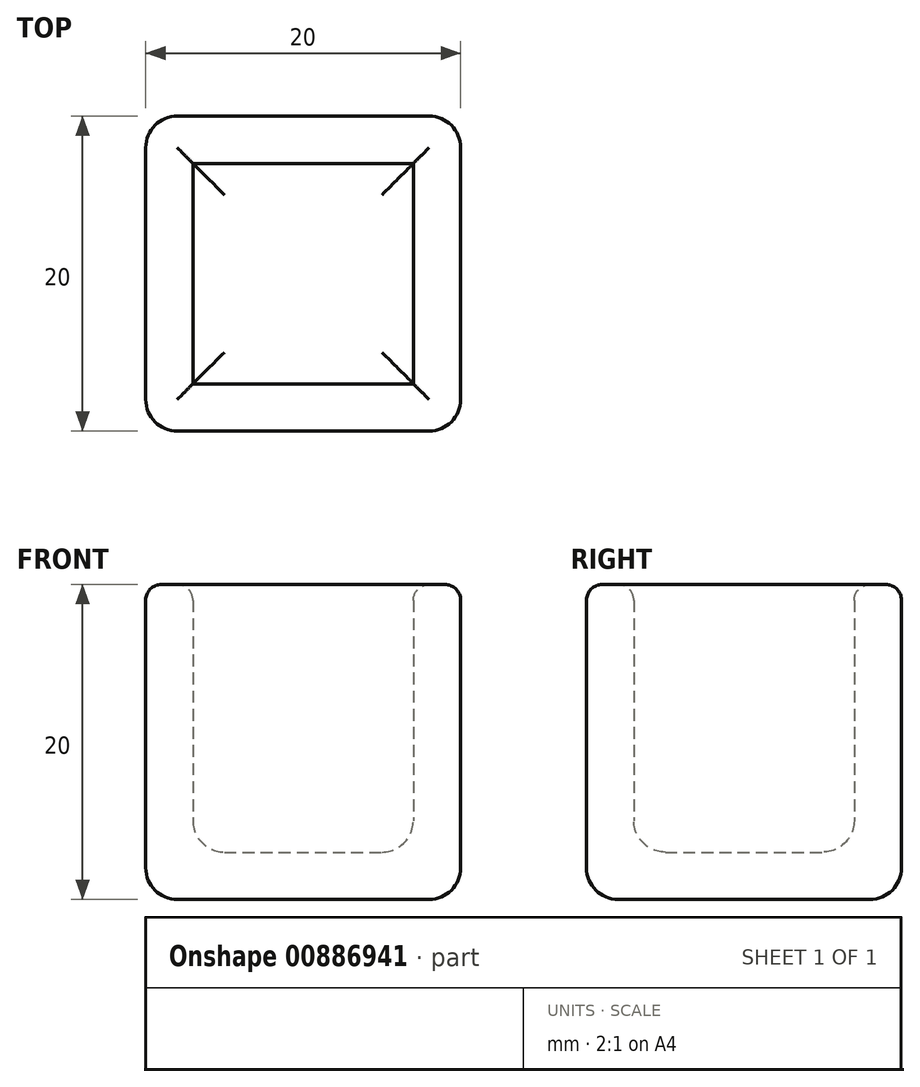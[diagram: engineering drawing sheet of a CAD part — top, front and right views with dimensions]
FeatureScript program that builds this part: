
annotation { "Feature Type Name" : "Feature", "Feature Type Description" : "" }
export const myFeature = defineFeature(function(context is Context, id is Id, definition is map)
    precondition{}
    {
        {
            var Q0;
            Q0=qCreatedBy(makeId("Top.planeOp"),FACE);
            var sketch = newSketch(context, id + "F0", { "sketchPlane" : qUnion([Q0])});
            skLineSegment(sketch, "E0.bottom", {"start": v(-8, 10) * mm, "end": v(8, 10) * mm});
            skLineSegment(sketch, "E0.top", {"start": v(-8, -10) * mm, "end": v(8, -10) * mm});
            skLineSegment(sketch, "E0.left", {"start": v(-10, 8) * mm, "end": v(-10, -8) * mm});
            skLineSegment(sketch, "E0.right", {"start": v(10, 8) * mm, "end": v(10, -8) * mm});
            skPoint(sketch, "E0.middle", {"position": v(0, 0) * mm});
            skPoint(sketch, "E1.visualSharp", {"position": v(-10, 10) * mm});
            skArc(sketch, "E1.filletArc", {"start": v(-8, 10) * mm, "mid": v(-9.41, 9.41) * mm, "end": v(-10, 8) * mm});
            skPoint(sketch, "E2.visualSharp", {"position": v(10, 10) * mm});
            skArc(sketch, "E2.filletArc", {"start": v(10, 8) * mm, "mid": v(9.41, 9.41) * mm, "end": v(8, 10) * mm});
            skPoint(sketch, "E3.visualSharp", {"position": v(10, -10) * mm});
            skArc(sketch, "E3.filletArc", {"start": v(8, -10) * mm, "mid": v(9.41, -9.41) * mm, "end": v(10, -8) * mm});
            skPoint(sketch, "E4.visualSharp", {"position": v(-10, -10) * mm});
            skArc(sketch, "E4.filletArc", {"start": v(-10, -8) * mm, "mid": v(-9.41, -9.41) * mm, "end": v(-8, -10) * mm});
            skSolve(sketch);
        }
        {
            var Q0;
            Q0=makeQuery(id+"F0.imprint","IMPRINT",FACE,{"disambiguationData":[TD([[makeQuery(id+"F0.imprint","IMPRINT",EDGE,{"derivedFrom":sQuery(id+"F0.wireOp",EDGE,"E0.bottom")}),-1.0]])]});
            extrude(context, id + "F1", {"entities" : qUnion([Q0]), "depth" : 20 * mm, "offsetDistance" : 25 * mm});
        }
        {
            var Q0;
            Q0=makeQuery(id+"F1.opExtrude","CAP_EDGE",EDGE,{"disambiguationData":[OSD([sQuery(id+"F0.wireOp",EDGE,"E0.top")])],"isStart":true});
            fillet(context, id + "F2", {"entities" : qUnion([Q0]), "radius" : 2 * mm, "tangentPropagation" : true, "allowEdgeOverflow" : false});
        }
        {
            var Q0;
            Q0=makeQuery(id+"F1.opExtrude","CAP_FACE",FACE,{"disambiguationData":[OSD([sQuery(id+"F0.wireOp",EDGE,"E0.bottom"),sQuery(id+"F0.wireOp",EDGE,"E0.top"),sQuery(id+"F0.wireOp",EDGE,"E0.left"),sQuery(id+"F0.wireOp",EDGE,"E0.right"),sQuery(id+"F0.wireOp",EDGE,"E1.filletArc"),sQuery(id+"F0.wireOp",EDGE,"E2.filletArc"),sQuery(id+"F0.wireOp",EDGE,"E3.filletArc"),sQuery(id+"F0.wireOp",EDGE,"E4.filletArc")])],"isStart":false});
            shell(context, id + "F3", {"entities" : qUnion([Q0]), "thickness" : 3 * mm});
        }
        {
            var Q0;
            Q0=makeQuery(id+"F1.opExtrude","CAP_EDGE",EDGE,{"disambiguationData":[OSD([sQuery(id+"F0.wireOp",EDGE,"E0.left")])],"isStart":false});
            var Q1;
            Q1=makeQuery(id+"F3.opShell","OFFSET_EDGE",EDGE,{"disambiguationData":[OSD([sQuery(id+"F0.wireOp",EDGE,"E0.right")])]});
            var Q2;
            Q2=makeQuery(id+"F3.opShell","OFFSET_EDGE",EDGE,{"disambiguationData":[OSD([sQuery(id+"F0.wireOp",EDGE,"E0.bottom")])]});
            var Q3;
            Q3=makeQuery(id+"F3.opShell","OFFSET_EDGE",EDGE,{"disambiguationData":[OSD([sQuery(id+"F0.wireOp",EDGE,"E0.left")])]});
            var Q4;
            Q4=makeQuery(id+"F3.opShell","OFFSET_EDGE",EDGE,{"disambiguationData":[OSD([sQuery(id+"F0.wireOp",EDGE,"E0.top")])]});
            fillet(context, id + "F4", {"entities" : qUnion([Q0, Q1, Q2, Q3, Q4]), "radius" : 1 * mm, "tangentPropagation" : true, "allowEdgeOverflow" : false});
        }
        {
            var Q0;
            {var subQ0=sQuery(id+"F0.wireOp",EDGE,"E4.filletArc");var subQ1=sQuery(id+"F0.wireOp",EDGE,"E3.filletArc");var subQ2=sQuery(id+"F0.wireOp",EDGE,"E2.filletArc");var subQ3=sQuery(id+"F0.wireOp",EDGE,"E1.filletArc");var subQ4=sQuery(id+"F0.wireOp",EDGE,"E0.right");var subQ5=sQuery(id+"F0.wireOp",EDGE,"E0.left");var subQ6=sQuery(id+"F0.wireOp",EDGE,"E0.top");var subQ7=sQuery(id+"F0.wireOp",EDGE,"E0.bottom");var subQ8=makeQuery(id+"F1.opExtrude","CAP_EDGE",EDGE,{"disambiguationData":[OSD([subQ7])],"isStart":true});Q0=makeQuery(id+"F3.opShell","OFFSET_EDGE",EDGE,{"disambiguationData":[OSD([subQ7,subQ6,subQ5,subQ4,subQ3,subQ2,subQ1,subQ0]),TDD([makeQuery(id+"F2.opFillet","BLEND_EDGE",EDGE,{"blendedFrom":[subQ8,makeQuery(id+"F1.opExtrude","SWEPT_FACE",FACE,{"disambiguationData":[OSD([subQ7])]})],"blendedInto":[makeQuery(id+"F1.opExtrude","SWEPT_FACE",FACE,{"disambiguationData":[OSD([subQ7])]})]}),makeQuery(id+"F2.opFillet","BLEND_EDGE",EDGE,{"blendedFrom":[subQ8,makeQuery(id+"F1.opExtrude","CAP_FACE",FACE,{"disambiguationData":[OSD([subQ7,subQ6,subQ5,subQ4,subQ3,subQ2,subQ1,subQ0])],"isStart":true})],"blendedInto":[makeQuery(id+"F1.opExtrude","CAP_FACE",FACE,{"disambiguationData":[OSD([subQ7,subQ6,subQ5,subQ4,subQ3,subQ2,subQ1,subQ0])],"isStart":true})]})])]});}
            var Q1;
            {var subQ0=sQuery(id+"F0.wireOp",EDGE,"E0.right");var subQ1=makeQuery(id+"F1.opExtrude","CAP_EDGE",EDGE,{"disambiguationData":[OSD([subQ0])],"isStart":true});var subQ2=sQuery(id+"F0.wireOp",EDGE,"E4.filletArc");var subQ3=sQuery(id+"F0.wireOp",EDGE,"E3.filletArc");var subQ4=sQuery(id+"F0.wireOp",EDGE,"E2.filletArc");var subQ5=sQuery(id+"F0.wireOp",EDGE,"E1.filletArc");var subQ6=sQuery(id+"F0.wireOp",EDGE,"E0.left");var subQ7=sQuery(id+"F0.wireOp",EDGE,"E0.top");var subQ8=sQuery(id+"F0.wireOp",EDGE,"E0.bottom");Q1=makeQuery(id+"F3.opShell","OFFSET_EDGE",EDGE,{"disambiguationData":[OSD([subQ8,subQ7,subQ6,subQ0,subQ5,subQ4,subQ3,subQ2]),TDD([makeQuery(id+"F2.opFillet","BLEND_EDGE",EDGE,{"blendedFrom":[subQ1,makeQuery(id+"F1.opExtrude","CAP_FACE",FACE,{"disambiguationData":[OSD([subQ8,subQ7,subQ6,subQ0,subQ5,subQ4,subQ3,subQ2])],"isStart":true})],"blendedInto":[makeQuery(id+"F1.opExtrude","CAP_FACE",FACE,{"disambiguationData":[OSD([subQ8,subQ7,subQ6,subQ0,subQ5,subQ4,subQ3,subQ2])],"isStart":true})]}),makeQuery(id+"F2.opFillet","BLEND_EDGE",EDGE,{"blendedFrom":[subQ1,makeQuery(id+"F1.opExtrude","SWEPT_FACE",FACE,{"disambiguationData":[OSD([subQ0])]})],"blendedInto":[makeQuery(id+"F1.opExtrude","SWEPT_FACE",FACE,{"disambiguationData":[OSD([subQ0])]})]})])]});}
            var Q2;
            {var subQ0=sQuery(id+"F0.wireOp",EDGE,"E0.top");var subQ1=makeQuery(id+"F1.opExtrude","CAP_EDGE",EDGE,{"disambiguationData":[OSD([subQ0])],"isStart":true});var subQ2=sQuery(id+"F0.wireOp",EDGE,"E4.filletArc");var subQ3=sQuery(id+"F0.wireOp",EDGE,"E3.filletArc");var subQ4=sQuery(id+"F0.wireOp",EDGE,"E2.filletArc");var subQ5=sQuery(id+"F0.wireOp",EDGE,"E1.filletArc");var subQ6=sQuery(id+"F0.wireOp",EDGE,"E0.right");var subQ7=sQuery(id+"F0.wireOp",EDGE,"E0.left");var subQ8=sQuery(id+"F0.wireOp",EDGE,"E0.bottom");Q2=makeQuery(id+"F3.opShell","OFFSET_EDGE",EDGE,{"disambiguationData":[OSD([subQ8,subQ0,subQ7,subQ6,subQ5,subQ4,subQ3,subQ2]),TDD([makeQuery(id+"F2.opFillet","BLEND_EDGE",EDGE,{"blendedFrom":[subQ1,makeQuery(id+"F1.opExtrude","CAP_FACE",FACE,{"disambiguationData":[OSD([subQ8,subQ0,subQ7,subQ6,subQ5,subQ4,subQ3,subQ2])],"isStart":true})],"blendedInto":[makeQuery(id+"F1.opExtrude","CAP_FACE",FACE,{"disambiguationData":[OSD([subQ8,subQ0,subQ7,subQ6,subQ5,subQ4,subQ3,subQ2])],"isStart":true})]}),makeQuery(id+"F2.opFillet","BLEND_EDGE",EDGE,{"blendedFrom":[subQ1,makeQuery(id+"F1.opExtrude","SWEPT_FACE",FACE,{"disambiguationData":[OSD([subQ0])]})],"blendedInto":[makeQuery(id+"F1.opExtrude","SWEPT_FACE",FACE,{"disambiguationData":[OSD([subQ0])]})]})])]});}
            var Q3;
            {var subQ0=sQuery(id+"F0.wireOp",EDGE,"E0.left");var subQ1=makeQuery(id+"F1.opExtrude","CAP_EDGE",EDGE,{"disambiguationData":[OSD([subQ0])],"isStart":true});var subQ2=sQuery(id+"F0.wireOp",EDGE,"E4.filletArc");var subQ3=sQuery(id+"F0.wireOp",EDGE,"E3.filletArc");var subQ4=sQuery(id+"F0.wireOp",EDGE,"E2.filletArc");var subQ5=sQuery(id+"F0.wireOp",EDGE,"E1.filletArc");var subQ6=sQuery(id+"F0.wireOp",EDGE,"E0.right");var subQ7=sQuery(id+"F0.wireOp",EDGE,"E0.top");var subQ8=sQuery(id+"F0.wireOp",EDGE,"E0.bottom");Q3=makeQuery(id+"F3.opShell","OFFSET_EDGE",EDGE,{"disambiguationData":[OSD([subQ8,subQ7,subQ0,subQ6,subQ5,subQ4,subQ3,subQ2]),TDD([makeQuery(id+"F2.opFillet","BLEND_EDGE",EDGE,{"blendedFrom":[subQ1,makeQuery(id+"F1.opExtrude","CAP_FACE",FACE,{"disambiguationData":[OSD([subQ8,subQ7,subQ0,subQ6,subQ5,subQ4,subQ3,subQ2])],"isStart":true})],"blendedInto":[makeQuery(id+"F1.opExtrude","CAP_FACE",FACE,{"disambiguationData":[OSD([subQ8,subQ7,subQ0,subQ6,subQ5,subQ4,subQ3,subQ2])],"isStart":true})]}),makeQuery(id+"F2.opFillet","BLEND_EDGE",EDGE,{"blendedFrom":[subQ1,makeQuery(id+"F1.opExtrude","SWEPT_FACE",FACE,{"disambiguationData":[OSD([subQ0])]})],"blendedInto":[makeQuery(id+"F1.opExtrude","SWEPT_FACE",FACE,{"disambiguationData":[OSD([subQ0])]})]})])]});}
            fillet(context, id + "F5", {"entities" : qUnion([Q0, Q1, Q2, Q3]), "radius" : 2 * mm, "tangentPropagation" : true, "allowEdgeOverflow" : false});
        }
    });
